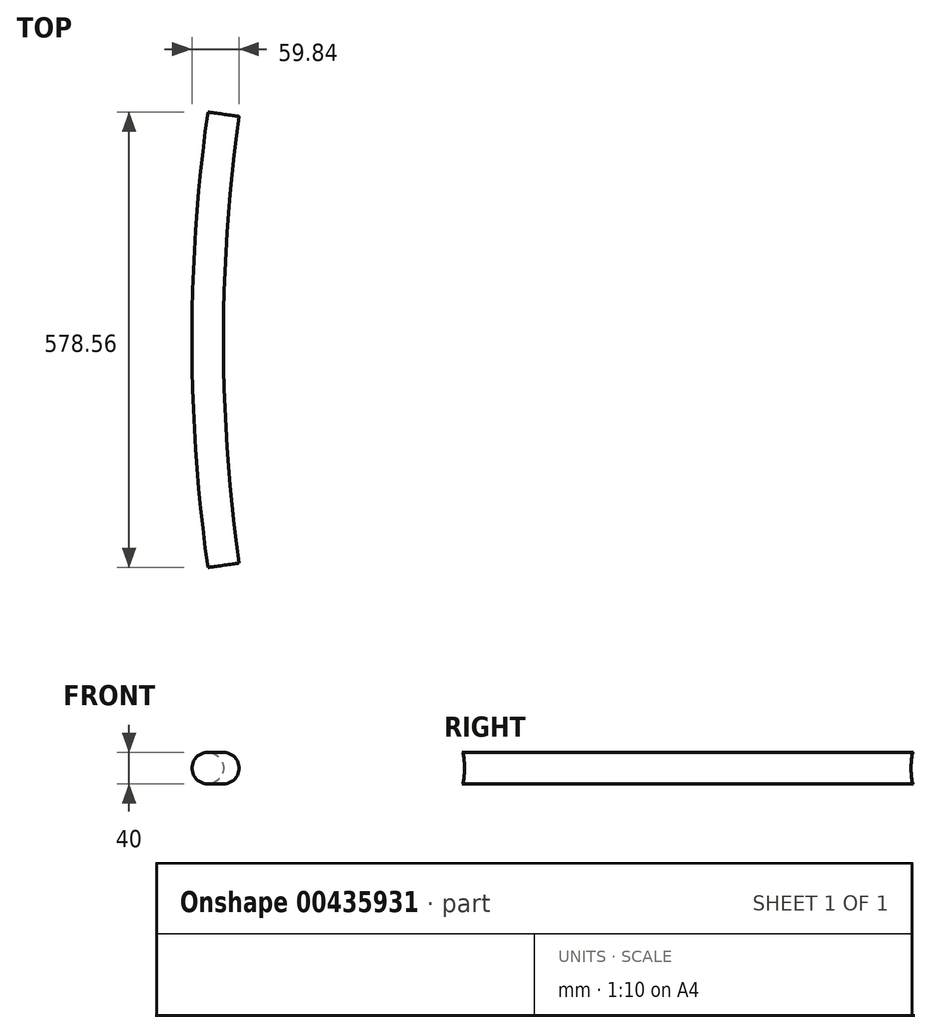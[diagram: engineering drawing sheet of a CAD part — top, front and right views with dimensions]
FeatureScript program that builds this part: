
annotation { "Feature Type Name" : "Feature", "Feature Type Description" : "" }
export const myFeature = defineFeature(function(context is Context, id is Id, definition is map)
    precondition{}
    {
        {
            var Q0;
            Q0=qCreatedBy(makeId("Front.planeOp"),FACE);
            var sketch = newSketch(context, id + "F0", { "sketchPlane" : qUnion([Q0])});
            skCircle(sketch, "E0", {"center": v(0, 0) * mm, "radius": 20 * mm});
            skSolve(sketch);
        }
        {
            var Q0;
            Q0=qCreatedBy(makeId("Front.planeOp"),FACE);
            var sketch = newSketch(context, id + "F1", { "sketchPlane" : qUnion([Q0])});
            skLineSegment(sketch, "E1", {"start": v(2058.54, 0) * mm, "end": v(2058.54, -311.27) * mm});
            skSolve(sketch);
        }
        {
            var Q0;
            Q0=makeQuery(id+"F0.imprint","IMPRINT",FACE,{"disambiguationData":[TD([[makeQuery(id+"F0.imprint","IMPRINT",EDGE,{"derivedFrom":sQuery(id+"F0.wireOp",EDGE,"E0")}),1.0]])]});
            var Q1;
            Q1=sQuery(id+"F1.wireOp",EDGE,"E1");
            revolve(context, id + "F2", {"entities" : qUnion([Q0]), "axis" : qUnion([Q1]), "revolveType" : RevolveType.SYMMETRIC, "angle" : 16 * degree});
        }
    });
